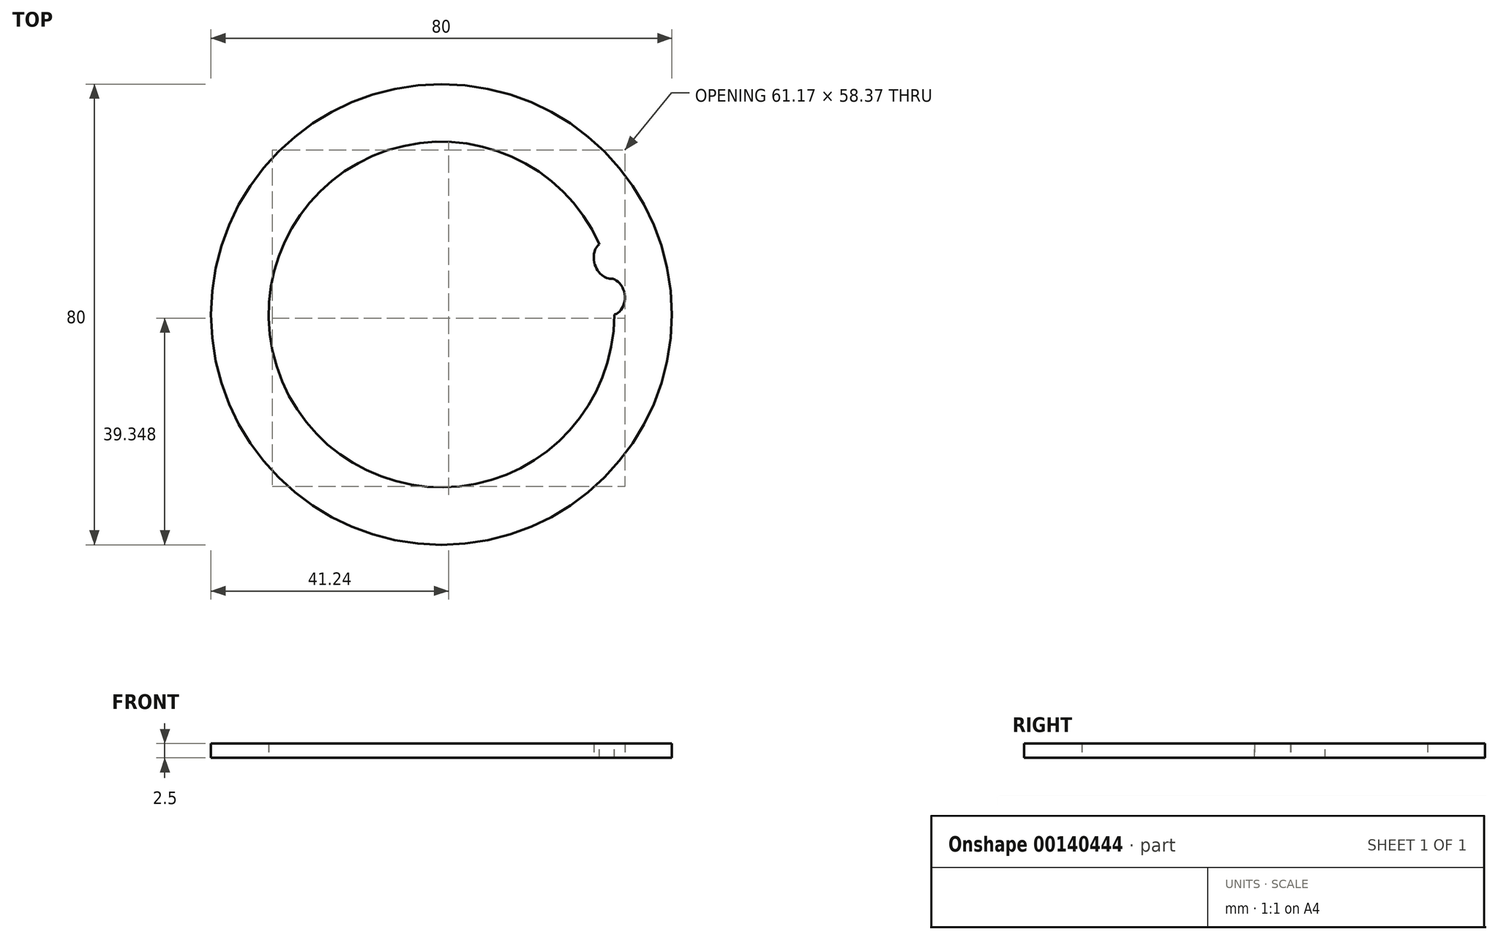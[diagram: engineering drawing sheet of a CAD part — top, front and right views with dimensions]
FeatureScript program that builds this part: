
annotation { "Feature Type Name" : "Feature", "Feature Type Description" : "" }
export const myFeature = defineFeature(function(context is Context, id is Id, definition is map)
    precondition{}
    {
        {
            assignVariable(context, id + "F0", {"name" : "t", "anyValue" : 2.5});
        }
        {
            var Q0;
            Q0=qCreatedBy(makeId("Top.planeOp"),FACE);
            var sketch = newSketch(context, id + "F1", { "sketchPlane" : qUnion([Q0])});
            skCircle(sketch, "E0", {"center": v(0, 0) * mm, "radius": 30 * mm});
            skCircle(sketch, "E1", {"center": v(0, 0) * mm, "radius": 40 * mm});
            skSolve(sketch);
        }
        {
            var Q0;
            Q0=qSketchRegion(id+"F1",true);
            extrude(context, id + "F2", {"entities" : qUnion([Q0]), "depth" : (getVariable(context, 't')) * mm});
        }
        {
            var Q0;
            Q0=makeQuery(id+"F2.opExtrude","CAP_FACE",FACE,{"disambiguationData":[OSD([sQuery(id+"F1.wireOp",EDGE,"E0")])],"isStart":false});
            var sketch = newSketch(context, id + "F3", { "sketchPlane" : qUnion([Q0])});
            skLineSegment(sketch, "E2", {"start": v(0, 0) * mm, "end": v(29.34, 6.24) * mm, "construction": true});
            skLineSegment(sketch, "E3", {"start": v(29.34, 6.24) * mm, "end": v(31.3, 6.65) * mm, "construction": true});
            skPoint(sketch, "E4", {"position": v(30.32, 6.45) * mm});
            skCircle(sketch, "E5", {"center": v(30.32, 6.45) * mm, "radius": 1 * mm, "construction": true});
            skLineSegment(sketch, "E6", {"start": v(30, 0) * mm, "end": v(31, 0) * mm, "construction": true});
            skLineSegment(sketch, "E7", {"start": v(30.32, 6.45) * mm, "end": v(29.58, 5.78) * mm, "construction": true});
            skLineSegment(sketch, "E8", {"start": v(30.32, 6.45) * mm, "end": v(31.07, 7.11) * mm, "construction": true});
            skLineSegment(sketch, "E9", {"start": v(30.32, 6.45) * mm, "end": v(29.37, 6.75) * mm, "construction": true});
            skLineSegment(sketch, "E10", {"start": v(30.32, 6.45) * mm, "end": v(31.27, 6.14) * mm, "construction": true});
            skLineSegment(sketch, "E11", {"start": v(30.32, 6.45) * mm, "end": v(30.01, 5.5) * mm, "construction": true});
            skLineSegment(sketch, "E12", {"start": v(30.32, 6.45) * mm, "end": v(30.53, 5.47) * mm, "construction": true});
            skLineSegment(sketch, "E13", {"start": v(30.32, 6.45) * mm, "end": v(31, 5.7) * mm, "construction": true});
            skLineSegment(sketch, "E14", {"start": v(30.32, 6.45) * mm, "end": v(30.63, 7.4) * mm, "construction": true});
            skLineSegment(sketch, "E15", {"start": v(30.32, 6.45) * mm, "end": v(30.11, 7.42) * mm, "construction": true});
            skLineSegment(sketch, "E16", {"start": v(30.32, 6.45) * mm, "end": v(29.65, 7.19) * mm, "construction": true});
            skArc(sketch, "E17", {"start": v(31, 0) * mm, "mid": v(30.83, 3.24) * mm, "end": v(30.32, 6.45) * mm, "construction": true});
            skLineSegment(sketch, "E18", {"start": v(30.43, 5.92) * mm, "end": v(0, 0) * mm, "construction": true});
            skLineSegment(sketch, "E19", {"start": v(0, 0) * mm, "end": v(30.53, 5.38) * mm, "construction": true});
            skLineSegment(sketch, "E20", {"start": v(0, 0) * mm, "end": v(30.62, 4.85) * mm, "construction": true});
            skLineSegment(sketch, "E21", {"start": v(0, 0) * mm, "end": v(30.7, 4.31) * mm, "construction": true});
            skLineSegment(sketch, "E22", {"start": v(0, 0) * mm, "end": v(30.77, 3.78) * mm, "construction": true});
            skLineSegment(sketch, "E23", {"start": v(0, 0) * mm, "end": v(30.83, 3.24) * mm, "construction": true});
            skLineSegment(sketch, "E24", {"start": v(0, 0) * mm, "end": v(30.88, 2.7) * mm, "construction": true});
            skLineSegment(sketch, "E25", {"start": v(0, 0) * mm, "end": v(30.92, 2.16) * mm, "construction": true});
            skLineSegment(sketch, "E26", {"start": v(0, 0) * mm, "end": v(30.96, 1.62) * mm, "construction": true});
            skLineSegment(sketch, "E27", {"start": v(0, 0) * mm, "end": v(30.98, 1.08) * mm, "construction": true});
            skLineSegment(sketch, "E28", {"start": v(0, 0) * mm, "end": v(31, 0.54) * mm, "construction": true});
            skLineSegment(sketch, "E29", {"start": v(0, 0) * mm, "end": v(31, 0) * mm, "construction": true});
            skLineSegment(sketch, "E30", {"start": v(31, 0) * mm, "end": v(31.87, 0) * mm, "construction": true});
            skArc(sketch, "E31", {"start": v(29.37, 6.75) * mm, "mid": v(29.95, 3.4) * mm, "end": v(30.14, 0) * mm, "construction": true});
            skArc(sketch, "E32", {"start": v(29.65, 7.19) * mm, "mid": v(30.3, 3.62) * mm, "end": v(30.51, 0) * mm, "construction": true});
            skArc(sketch, "E33", {"start": v(30.11, 7.42) * mm, "mid": v(30.79, 3.74) * mm, "end": v(31.02, 0) * mm, "construction": true});
            skArc(sketch, "E34", {"start": v(30.63, 7.4) * mm, "mid": v(31.3, 3.72) * mm, "end": v(31.51, 0) * mm, "construction": true});
            skArc(sketch, "E35", {"start": v(31.07, 7.11) * mm, "mid": v(31.67, 3.58) * mm, "end": v(31.87, 0) * mm, "construction": true});
            skPoint(sketch, "E36", {"position": v(29.95, 5.82) * mm});
            skPoint(sketch, "E37", {"position": v(30.43, 5.92) * mm});
            skLineSegment(sketch, "E38", {"start": v(30.43, 5.92) * mm, "end": v(29.48, 6.24) * mm, "construction": true});
            skLineSegment(sketch, "E39", {"start": v(30.53, 5.38) * mm, "end": v(29.89, 6.15) * mm, "construction": true});
            skLineSegment(sketch, "E40", {"start": v(30.62, 4.85) * mm, "end": v(30.46, 5.84) * mm, "construction": true});
            skLineSegment(sketch, "E41", {"start": v(30.7, 4.31) * mm, "end": v(31.07, 5.24) * mm, "construction": true});
            skArc(sketch, "E42", {"start": v(31.3, 6.65) * mm, "mid": v(31.82, 3.34) * mm, "end": v(32, 0) * mm, "construction": true});
            skLineSegment(sketch, "E43", {"start": v(30.77, 3.78) * mm, "end": v(31.57, 4.38) * mm, "construction": true});
            skLineSegment(sketch, "E44", {"start": v(30.83, 3.24) * mm, "end": v(31.82, 3.34) * mm, "construction": true});
            skLineSegment(sketch, "E45", {"start": v(30.88, 2.7) * mm, "end": v(31.79, 2.28) * mm, "construction": true});
            skLineSegment(sketch, "E46", {"start": v(30.92, 2.16) * mm, "end": v(31.48, 1.33) * mm, "construction": true});
            skLineSegment(sketch, "E47", {"start": v(30.96, 1.62) * mm, "end": v(31, 0.62) * mm, "construction": true});
            skLineSegment(sketch, "E48", {"start": v(30.98, 1.08) * mm, "end": v(30.51, 0.2) * mm, "construction": true});
            skLineSegment(sketch, "E49", {"start": v(31, 0.54) * mm, "end": v(30.14, 0.03) * mm, "construction": true});
            skFitSpline(sketch, "E50", {"points": [v(29.34, 6.24) * mm, v(29.48, 6.24) * mm, v(29.89, 6.15) * mm, v(30.46, 5.84) * mm, v(31.07, 5.24) * mm, v(31.57, 4.38) * mm, v(31.82, 3.34) * mm, v(31.79, 2.28) * mm, v(31.48, 1.33) * mm, v(31, 0.62) * mm, v(30.51, 0.2) * mm, v(30.14, 0.03) * mm, v(30, 0) * mm], "startDerivative": vector(3.74, 0.8) * mm, "endDerivative": vector(-3.82, 0) * mm});
            skArc(sketch, "E51.0", {"start": v(30, 0) * mm, "mid": v(29.84, 3.14) * mm, "end": v(29.34, 6.24) * mm});
            skArc(sketch, "E52", {"start": v(29.34, 6.24) * mm, "mid": v(29.4, 5.98) * mm, "end": v(29.45, 5.72) * mm});
            skArc(sketch, "E53", {"start": v(29.45, 5.72) * mm, "mid": v(29.5, 5.47) * mm, "end": v(29.54, 5.2) * mm});
            skSolve(sketch);
        }
        {
            var Q0;
            Q0 = qSketchRegion(id + "F3", true);
            var Q1;
            Q1=makeQuery(id+"F2.opExtrude","CAP_FACE",FACE,{"disambiguationData":[OSD([sQuery(id+"F1.wireOp",EDGE,"E0"),sQuery(id+"F1.wireOp",EDGE,"E1")])],"isStart":true});
            extrude(context, id + "F4", {"entities" : qUnion([Q0]), "operationType" : NewBodyOperationType.REMOVE, "endBound" : BoundingType.UP_TO_SURFACE, "oppositeDirection" : true, "endBoundEntityFace" : qUnion([Q1]), "depth" : 25 * mm});
        }
        {
            var Q0;
            {var subQ0=sQuery(id+"F3.wireOp",EDGE,"E51.0");Q0=makeQuery(id+"F3.imprint","IMPRINT",FACE,{"disambiguationData":[TD([[makeQuery(id+"F3.imprint","IMPRINT",EDGE,{"derivedFrom":subQ0}),1.0]])]});}
            var sketch = newSketch(context, id + "F5", { "sketchPlane" : qUnion([Q0])});
            skLineSegment(sketch, "E54.0", {"start": v(0, 0) * mm, "end": v(29.34, 6.24) * mm, "construction": true});
            skLineSegment(sketch, "E55.0.0", {"start": v(30, 0) * mm, "end": v(30, 0) * mm});
            skLineSegment(sketch, "E56", {"start": v(0, 0) * mm, "end": v(27.4, 12.2) * mm, "construction": true});
            skCircle(sketch, "E57", {"center": v(26.5, 11.8) * mm, "radius": 1 * mm, "construction": true});
            skArc(sketch, "E58", {"start": v(26.5, 11.8) * mm, "mid": v(27.58, 8.96) * mm, "end": v(28.37, 6.03) * mm, "construction": true});
            skLineSegment(sketch, "E59", {"start": v(26.5, 11.8) * mm, "end": v(26.9, 10.88) * mm, "construction": true});
            skArc(sketch, "E60", {"start": v(27.08, 12.6) * mm, "mid": v(28.33, 9.47) * mm, "end": v(29.22, 6.21) * mm, "construction": true});
            skArc(sketch, "E61", {"start": v(26.6, 12.79) * mm, "mid": v(27.93, 9.53) * mm, "end": v(28.87, 6.14) * mm, "construction": true});
            skArc(sketch, "E62", {"start": v(25.68, 12.38) * mm, "mid": v(26.98, 9.22) * mm, "end": v(27.9, 5.93) * mm, "construction": true});
            skArc(sketch, "E63", {"start": v(25.5, 11.9) * mm, "mid": v(26.68, 8.93) * mm, "end": v(27.52, 5.85) * mm, "construction": true});
            skArc(sketch, "E64", {"start": v(27.4, 12.2) * mm, "mid": v(27.51, 11.96) * mm, "end": v(27.62, 11.72) * mm});
            skLineSegment(sketch, "E65", {"start": v(27.62, 11.72) * mm, "end": v(0, 0) * mm, "construction": true});
            skArc(sketch, "E66", {"start": v(27.4, 12.2) * mm, "mid": v(28.53, 9.27) * mm, "end": v(29.34, 6.24) * mm});
            skLineSegment(sketch, "E67", {"start": v(0, 0) * mm, "end": v(27.82, 11.24) * mm, "construction": true});
            skLineSegment(sketch, "E68", {"start": v(0, 0) * mm, "end": v(28, 10.75) * mm, "construction": true});
            skLineSegment(sketch, "E69", {"start": v(0, 0) * mm, "end": v(28.2, 10.26) * mm, "construction": true});
            skLineSegment(sketch, "E70", {"start": v(0, 0) * mm, "end": v(28.37, 9.77) * mm, "construction": true});
            skLineSegment(sketch, "E71", {"start": v(0, 0) * mm, "end": v(28.53, 9.27) * mm, "construction": true});
            skLineSegment(sketch, "E72", {"start": v(0, 0) * mm, "end": v(28.69, 8.77) * mm, "construction": true});
            skLineSegment(sketch, "E73", {"start": v(0, 0) * mm, "end": v(28.84, 8.27) * mm, "construction": true});
            skLineSegment(sketch, "E74", {"start": v(28.98, 7.76) * mm, "end": v(0, 0) * mm, "construction": true});
            skLineSegment(sketch, "E75", {"start": v(0, 0) * mm, "end": v(29.1, 7.26) * mm, "construction": true});
            skLineSegment(sketch, "E76", {"start": v(0, 0) * mm, "end": v(29.23, 6.75) * mm, "construction": true});
            skLineSegment(sketch, "E77", {"start": v(26.7, 11.33) * mm, "end": v(27.3, 12.13) * mm, "construction": true});
            skLineSegment(sketch, "E78", {"start": v(26.89, 10.86) * mm, "end": v(27.03, 11.85) * mm, "construction": true});
            skArc(sketch, "E79", {"start": v(26.09, 12.7) * mm, "mid": v(27.44, 9.44) * mm, "end": v(28.38, 6.03) * mm, "construction": true});
            skLineSegment(sketch, "E80", {"start": v(27.07, 10.4) * mm, "end": v(26.72, 11.33) * mm, "construction": true});
            skLineSegment(sketch, "E81", {"start": v(27.25, 9.92) * mm, "end": v(26.49, 10.56) * mm, "construction": true});
            skLineSegment(sketch, "E82", {"start": v(27.42, 9.44) * mm, "end": v(26.44, 9.63) * mm, "construction": true});
            skLineSegment(sketch, "E83", {"start": v(27.58, 8.96) * mm, "end": v(26.63, 8.65) * mm, "construction": true});
            skArc(sketch, "E84", {"start": v(25.58, 11.39) * mm, "mid": v(26.63, 8.65) * mm, "end": v(27.39, 5.82) * mm, "construction": true});
            skLineSegment(sketch, "E85", {"start": v(27.73, 8.48) * mm, "end": v(27.05, 7.75) * mm, "construction": true});
            skLineSegment(sketch, "E86", {"start": v(27.88, 8) * mm, "end": v(27.63, 7.02) * mm, "construction": true});
            skLineSegment(sketch, "E87", {"start": v(28.14, 7.02) * mm, "end": v(28.83, 6.3) * mm, "construction": true});
            skLineSegment(sketch, "E88", {"start": v(28.26, 6.52) * mm, "end": v(29.21, 6.23) * mm, "construction": true});
            skFitSpline(sketch, "E89", {"points": [v(29.34, 6.24) * mm, v(29.21, 6.23) * mm, v(28.83, 6.3) * mm, v(27.63, 7.02) * mm, v(27.05, 7.75) * mm, v(26.63, 8.65) * mm, v(26.44, 9.63) * mm, v(26.49, 10.56) * mm, v(26.72, 11.33) * mm, v(27.03, 11.85) * mm, v(27.3, 12.13) * mm, v(27.4, 12.2) * mm], "startDerivative": vector(-3.54, -0.75) * mm, "endDerivative": vector(3.3, 1.47) * mm});
            skLineSegment(sketch, "E90", {"start": v(26.5, 11.8) * mm, "end": v(27.08, 12.6) * mm, "construction": true});
            skLineSegment(sketch, "E91", {"start": v(26.5, 11.8) * mm, "end": v(26.6, 12.79) * mm, "construction": true});
            skLineSegment(sketch, "E92", {"start": v(26.5, 11.8) * mm, "end": v(26.09, 12.7) * mm, "construction": true});
            skLineSegment(sketch, "E93", {"start": v(26.5, 11.8) * mm, "end": v(25.68, 12.38) * mm, "construction": true});
            skLineSegment(sketch, "E94", {"start": v(26.5, 11.8) * mm, "end": v(25.5, 11.9) * mm, "construction": true});
            skSolve(sketch);
        }
        {
            var Q0;
            Q0 = qSketchRegion(id + "F5", true);
            var Q1;
            Q1=makeQuery(id+"F2.opExtrude","CAP_FACE",FACE,{"disambiguationData":[OSD([sQuery(id+"F1.wireOp",EDGE,"E0"),sQuery(id+"F1.wireOp",EDGE,"E1")])],"isStart":true});
            extrude(context, id + "F6", {"entities" : qUnion([Q0]), "operationType" : NewBodyOperationType.ADD, "endBound" : BoundingType.UP_TO_SURFACE, "oppositeDirection" : true, "endBoundEntityFace" : qUnion([Q1]), "depth" : 25 * mm});
        }
    });
